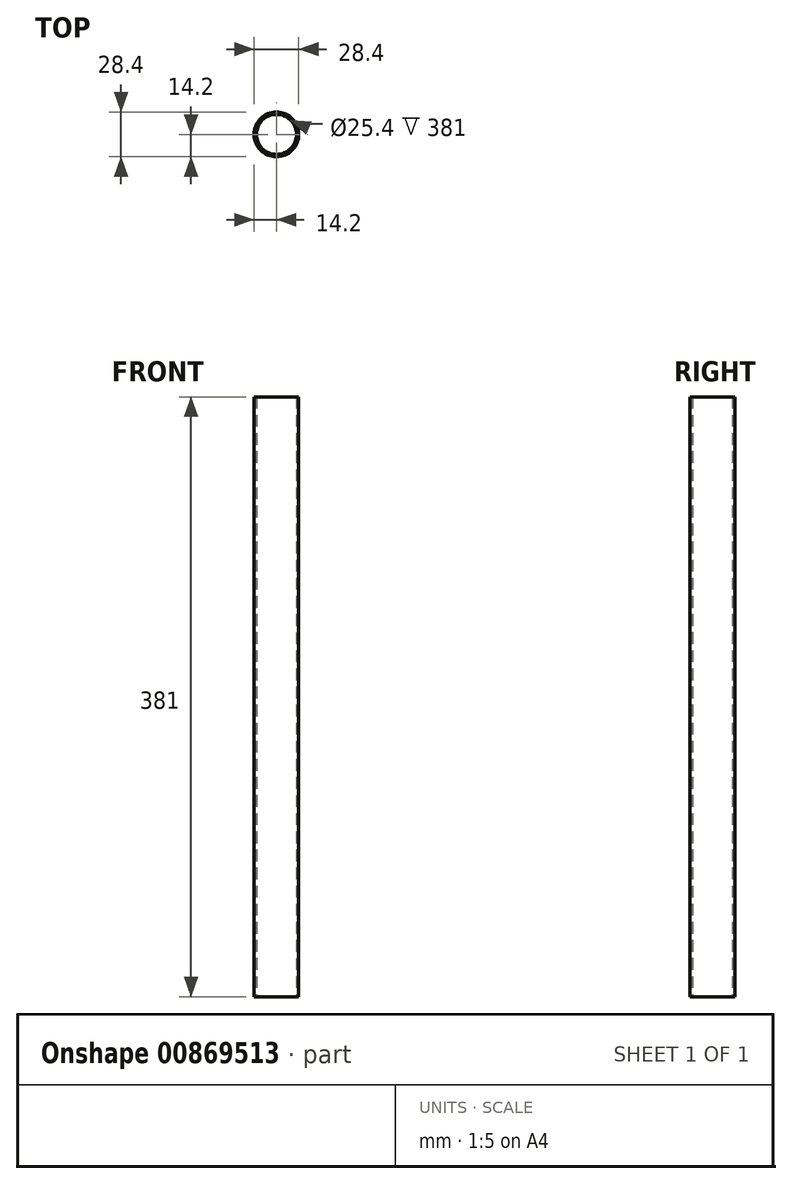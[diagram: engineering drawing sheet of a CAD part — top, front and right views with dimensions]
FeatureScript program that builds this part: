
annotation { "Feature Type Name" : "Feature", "Feature Type Description" : "" }
export const myFeature = defineFeature(function(context is Context, id is Id, definition is map)
    precondition{}
    {
        {
            var Q0;
            Q0=qCreatedBy(makeId("Top.planeOp"),FACE);
            var sketch = newSketch(context, id + "F0", { "sketchPlane" : qUnion([Q0])});
            skCircle(sketch, "E0", {"center": v(0, 0) * mm, "radius": 12.7 * mm});
            skCircle(sketch, "E1.0", {"center": v(0, 0) * mm, "radius": 14.2 * mm});
            skSolve(sketch);
        }
        {
            var Q0;
            Q0 = qSketchRegion(id + "F0", true);
            extrude(context, id + "F1", {"entities" : qUnion([Q0]), "depth" : 381 * mm, "offsetDistance" : 25.4 * mm});
        }
    });
